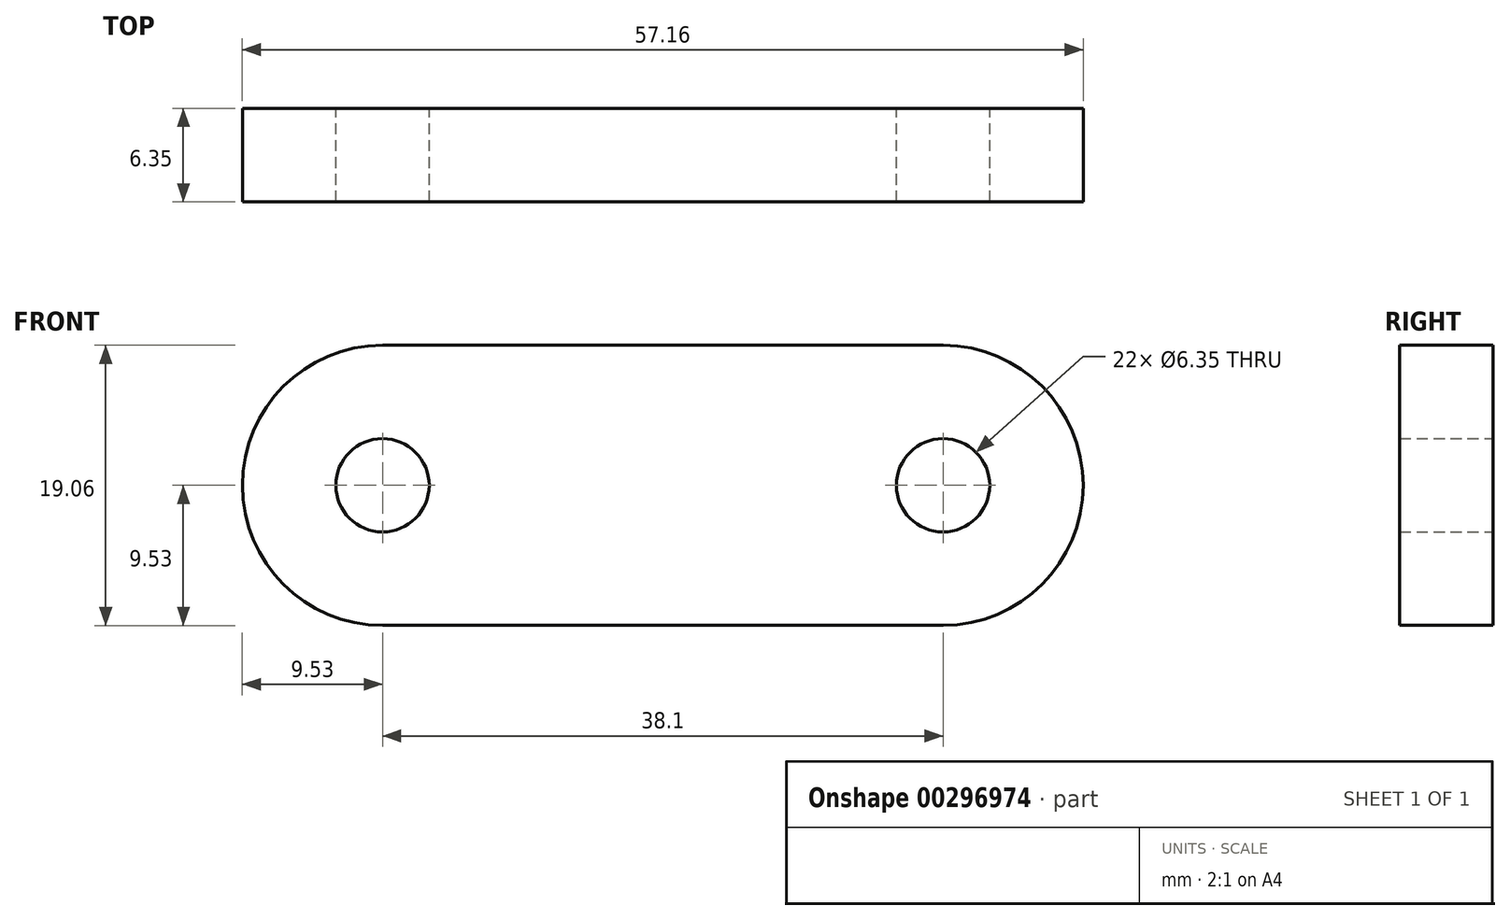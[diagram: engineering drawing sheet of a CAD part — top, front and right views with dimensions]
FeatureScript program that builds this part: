
annotation { "Feature Type Name" : "Feature", "Feature Type Description" : "" }
export const myFeature = defineFeature(function(context is Context, id is Id, definition is map)
    precondition{}
    {
        {
            var Q0;
            Q0=qCreatedBy(makeId("Front.planeOp"),FACE);
            var sketch = newSketch(context, id + "F0", { "sketchPlane" : qUnion([Q0])});
            skLineSegment(sketch, "E0.bottom", {"start": v(19.05, 9.53) * mm, "end": v(-19.05, 9.53) * mm});
            skLineSegment(sketch, "E0.top", {"start": v(19.05, -9.53) * mm, "end": v(-19.05, -9.53) * mm});
            skPoint(sketch, "E0.middle", {"position": v(0, 0) * mm});
            skCircle(sketch, "E1", {"center": v(-19.05, 0) * mm, "radius": 3.18 * mm});
            skCircle(sketch, "E2", {"center": v(19.05, 0) * mm, "radius": 3.18 * mm});
            skArc(sketch, "E3", {"start": v(-19.05, 9.53) * mm, "mid": v(-28.58, 0) * mm, "end": v(-19.05, -9.53) * mm});
            skArc(sketch, "E4", {"start": v(19.05, -9.53) * mm, "mid": v(28.57, 0) * mm, "end": v(19.05, 9.53) * mm});
            skSolve(sketch);
        }
        {
            var Q0;
            Q0=makeQuery(id+"F0.imprint","IMPRINT",FACE,{"disambiguationData":[TD([[makeQuery(id+"F0.imprint","IMPRINT",EDGE,{"derivedFrom":sQuery(id+"F0.wireOp",EDGE,"E0.bottom")}),1.0]])]});
            extrude(context, id + "F1", {"entities" : qUnion([Q0]), "depth" : 6.35 * mm});
        }
    });
